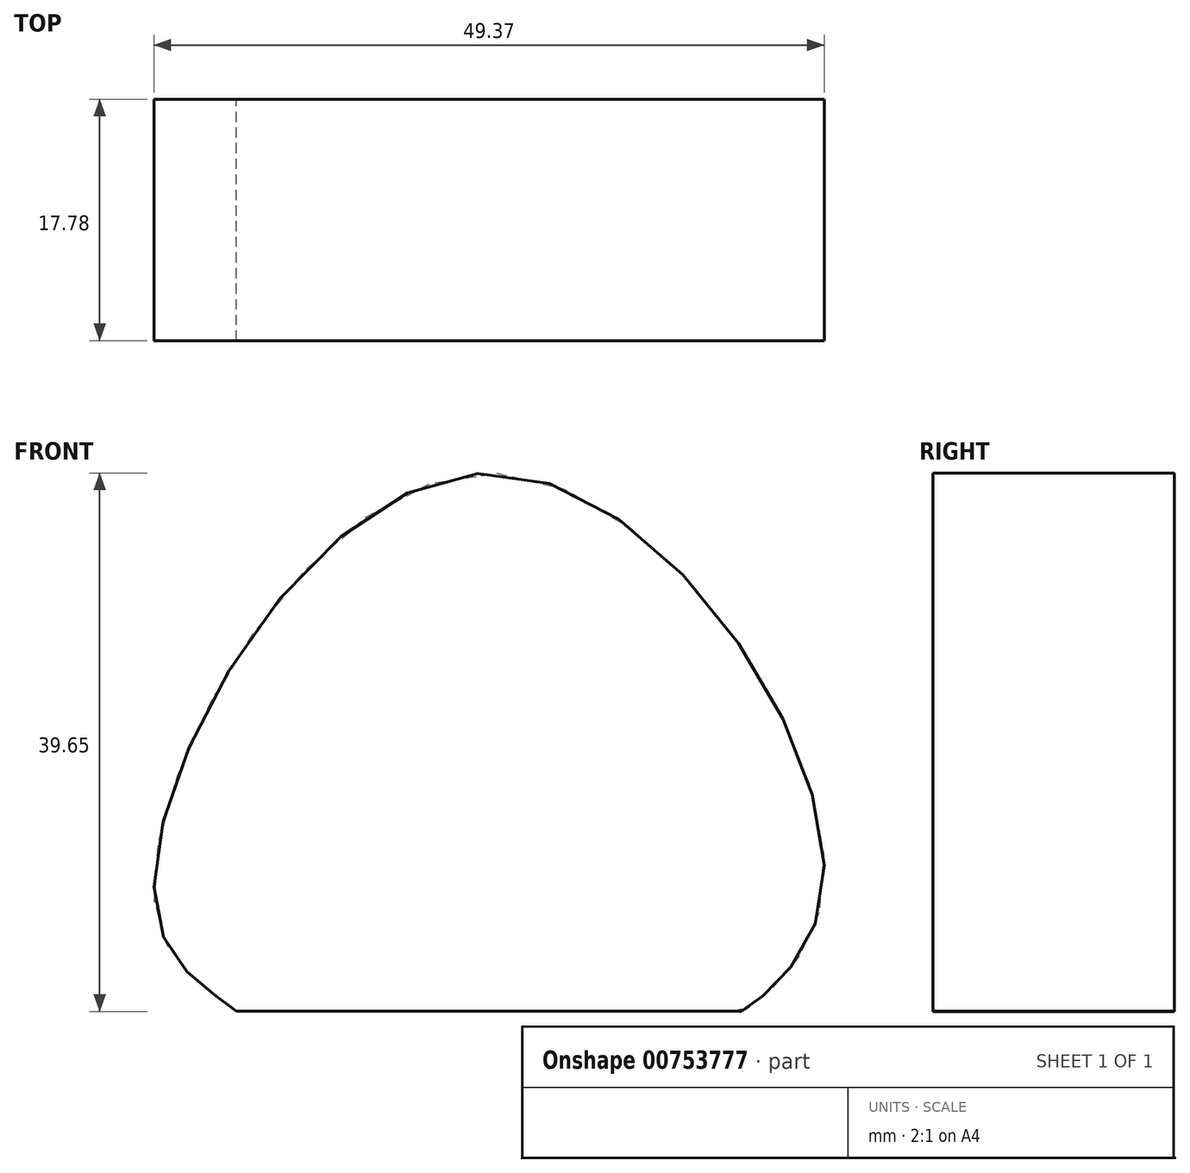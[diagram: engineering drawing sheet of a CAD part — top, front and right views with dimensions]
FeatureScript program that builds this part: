
annotation { "Feature Type Name" : "Feature", "Feature Type Description" : "" }
export const myFeature = defineFeature(function(context is Context, id is Id, definition is map)
    precondition{}
    {
        {
            var Q0;
            Q0=qCreatedBy(makeId("Front.planeOp"),FACE);
            var sketch = newSketch(context, id + "F0", { "sketchPlane" : qUnion([Q0])});
            skFitSpline(sketch, "E0", {"points": [v(-18.2, 0) * mm, v(-24.19, 7.8) * mm, v(0, 39.62) * mm, v(24.99, 8.6) * mm, v(19, 0) * mm, v(18.6, 0) * mm], "startDerivative": vector(-27.78, 23.82) * mm, "endDerivative": vector(-35.11, 0) * mm});
            skLineSegment(sketch, "E1", {"start": v(-18.2, 0) * mm, "end": v(18.6, 0) * mm});
            skSolve(sketch);
        }
        {
            var Q0;
            Q0 = qSketchRegion(id + "F0", true);
            extrude(context, id + "F1", {"entities" : qUnion([Q0]), "depth" : 17.78 * mm, "offsetDistance" : 25.4 * mm});
        }
    });
